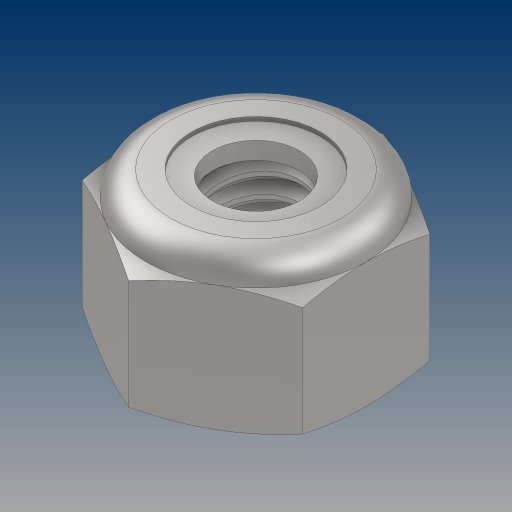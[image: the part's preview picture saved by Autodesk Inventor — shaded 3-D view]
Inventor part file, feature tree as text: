
AUTODESK INVENTOR PART (.ipt)
format: ipt  version: 2024.3 (Build 283343000, 343)  size: 322,048 bytes
history: native  units: in
note: dims shown in document units (in); Inventor stores cm internally (conversion verified against a paired STEP export)
features: other x1, revolve x1
ambient origin geometry x8: Origin, YZ Plane, XZ Plane, XY Plane, X Axis, Y Axis, Z Axis, Center Point
bodies: Solid1 (feature_tree), Solid2 (feature_tree)
feature tree (2):
  other  "Cut-Revolve4"
  revolve  "Revolve2"  [1 undecoded]
note: 1 required parameter value undecoded (feature->parameter linkage not recoverable at this tier; creation-order binding heuristic only, values carry confidence <= 0.55)
